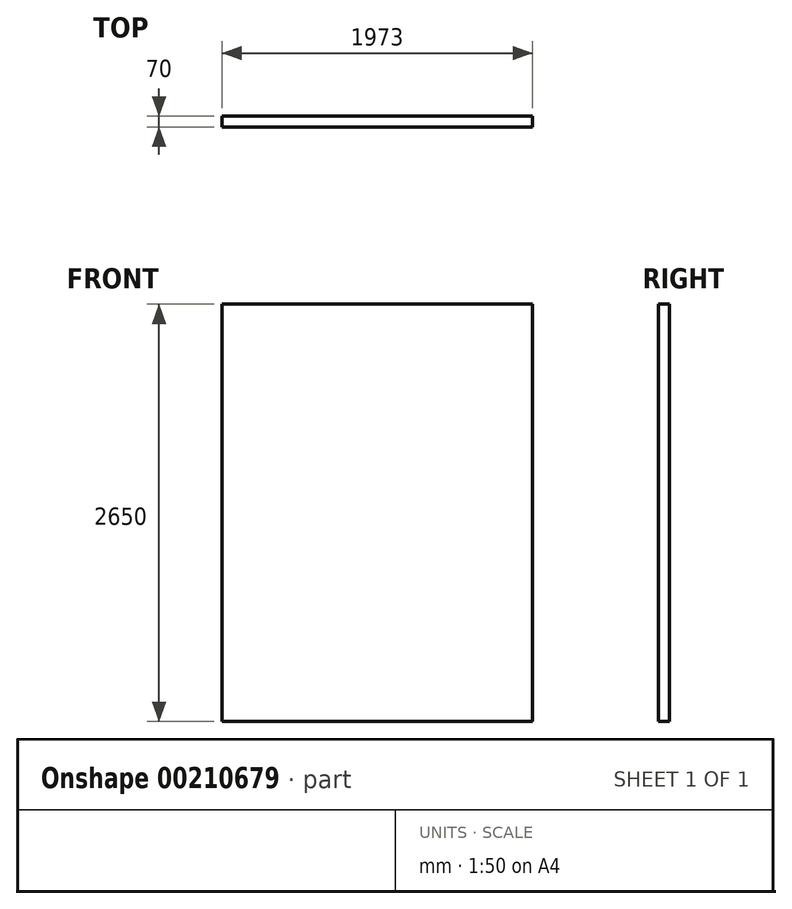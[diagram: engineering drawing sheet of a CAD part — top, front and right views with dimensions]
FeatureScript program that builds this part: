
annotation { "Feature Type Name" : "Feature", "Feature Type Description" : "" }
export const myFeature = defineFeature(function(context is Context, id is Id, definition is map)
    precondition{}
    {
        {
            var Q0;
            Q0=qCreatedBy(makeId("Front.planeOp"),FACE);
            var sketch = newSketch(context, id + "F0", { "sketchPlane" : qUnion([Q0])});
            skLineSegment(sketch, "E0.bottom", {"start": v(0, 0) * mm, "end": v(1973, 0) * mm});
            skLineSegment(sketch, "E0.left", {"start": v(0, 0) * mm, "end": v(0, 2650) * mm});
            skLineSegment(sketch, "E0.right", {"start": v(1973, 0) * mm, "end": v(1973, 2650) * mm});
            skLineSegment(sketch, "E1", {"start": v(0, 2650) * mm, "end": v(1973, 2650) * mm});
            skSolve(sketch);
        }
        {
            var Q0;
            Q0=makeQuery(id+"F0.imprint","IMPRINT",FACE,{"disambiguationData":[TD([[makeQuery(id+"F0.imprint","IMPRINT",EDGE,{"derivedFrom":sQuery(id+"F0.wireOp",EDGE,"E0.bottom")}),1.0]])]});
            extrude(context, id + "F1", {"entities" : qUnion([Q0]), "depth" : 70 * mm});
        }
    });
